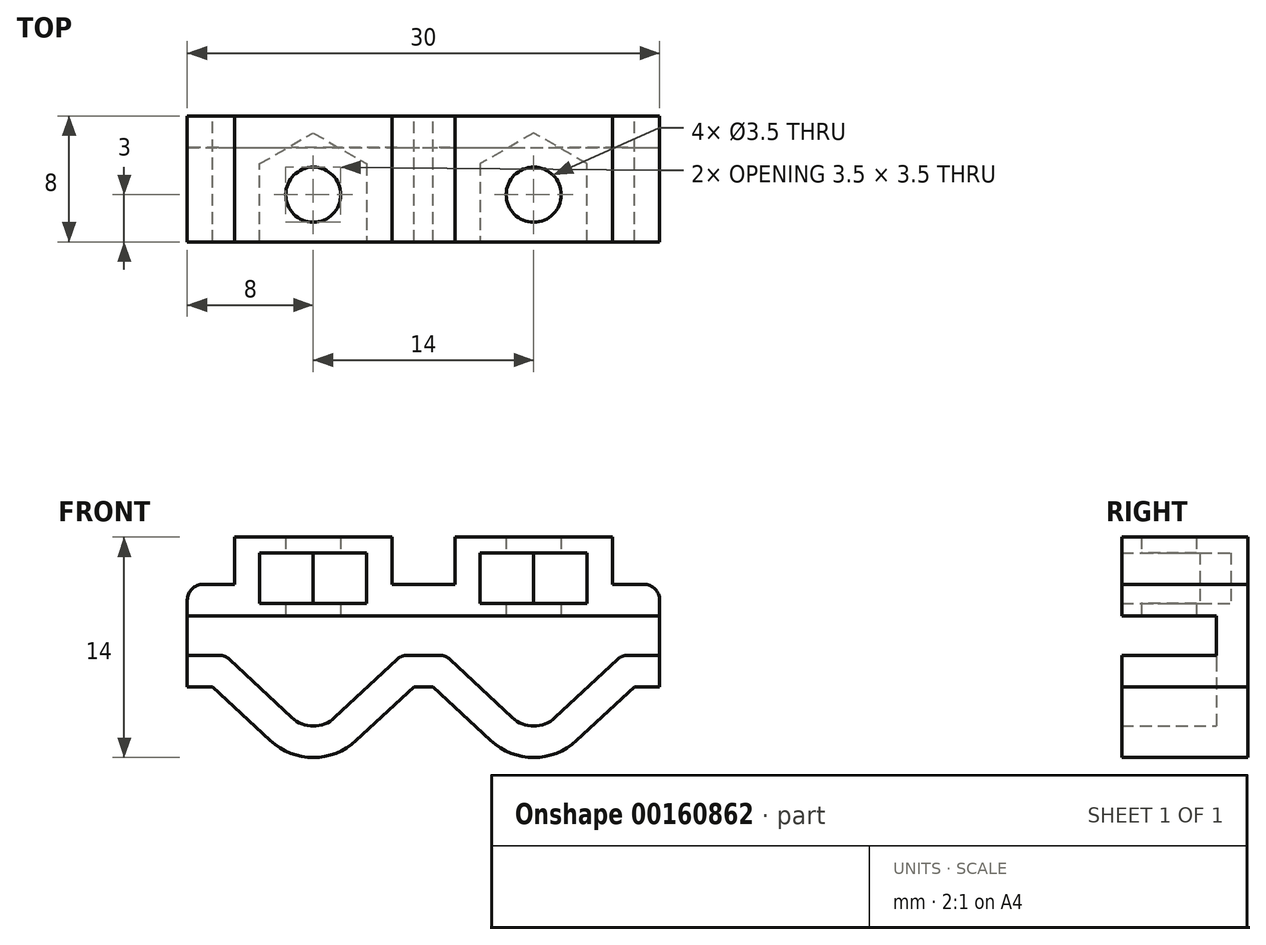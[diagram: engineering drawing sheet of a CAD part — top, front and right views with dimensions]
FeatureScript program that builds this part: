
annotation { "Feature Type Name" : "Feature", "Feature Type Description" : "" }
export const myFeature = defineFeature(function(context is Context, id is Id, definition is map)
    precondition{}
    {
        {
            var Q0;
            Q0=qCreatedBy(makeId("Front.planeOp"),FACE);
            var sketch = newSketch(context, id + "F0", { "sketchPlane" : qUnion([Q0])});
            skLineSegment(sketch, "E0", {"start": v(13, 0) * mm, "end": v(15, 0) * mm});
            skLineSegment(sketch, "E1", {"start": v(15, 0) * mm, "end": v(15, -2) * mm});
            skLineSegment(sketch, "E2", {"start": v(0, 0) * mm, "end": v(1, 0) * mm});
            skArc(sketch, "E3", {"start": v(13, 0) * mm, "mid": v(12.63, -0.07) * mm, "end": v(12.32, -0.27) * mm});
            skArc(sketch, "E4", {"start": v(1.68, -0.27) * mm, "mid": v(1.37, -0.07) * mm, "end": v(1, 0) * mm});
            skLineSegment(sketch, "E5", {"start": v(0, 2.5) * mm, "end": v(1, 2.5) * mm});
            skLineSegment(sketch, "E6", {"start": v(13, 2.5) * mm, "end": v(15, 2.5) * mm});
            skLineSegment(sketch, "E7", {"start": v(1, 2.5) * mm, "end": v(13, 2.5) * mm});
            skLineSegment(sketch, "E8", {"start": v(1.68, -0.27) * mm, "end": v(5.63, -3.96) * mm});
            skLineSegment(sketch, "E9", {"start": v(12.32, -0.27) * mm, "end": v(8.37, -3.96) * mm});
            skArc(sketch, "E10", {"start": v(5.63, -3.96) * mm, "mid": v(7, -4.5) * mm, "end": v(8.37, -3.96) * mm});
            skPoint(sketch, "E11", {"position": v(7, -4.5) * mm});
            skLineSegment(sketch, "E12", {"start": v(15, 2.5) * mm, "end": v(15, 3.5) * mm});
            skLineSegment(sketch, "E13", {"start": v(14, 4.5) * mm, "end": v(12, 4.5) * mm});
            skPoint(sketch, "E14.visualSharp", {"position": v(15, 4.5) * mm});
            skArc(sketch, "E14.filletArc", {"start": v(15, 3.5) * mm, "mid": v(14.7, 4.2) * mm, "end": v(14, 4.5) * mm});
            skLineSegment(sketch, "E15", {"start": v(2, 4.5) * mm, "end": v(2, 7.5) * mm});
            skLineSegment(sketch, "E16", {"start": v(2, 7.5) * mm, "end": v(12, 7.5) * mm});
            skLineSegment(sketch, "E17", {"start": v(12, 7.5) * mm, "end": v(12, 4.5) * mm});
            skPoint(sketch, "E18", {"position": v(7, 7.5) * mm});
            skLineSegment(sketch, "E19.trimOffspring", {"start": v(2, 4.5) * mm, "end": v(0, 4.5) * mm});
            skArc(sketch, "E20.0", {"start": v(4.27, -5.42) * mm, "mid": v(7, -6.5) * mm, "end": v(9.73, -5.42) * mm});
            skLineSegment(sketch, "E21", {"start": v(9.73, -5.42) * mm, "end": v(13.4, -2) * mm});
            skLineSegment(sketch, "E22", {"start": v(4.27, -5.42) * mm, "end": v(0.6, -2) * mm});
            skLineSegment(sketch, "E23", {"start": v(15, -2) * mm, "end": v(13.4, -2) * mm});
            skLineSegment(sketch, "E24", {"start": v(0, -2) * mm, "end": v(0.6, -2) * mm});
            skLineSegment(sketch, "E25", {"start": v(0, 2.5) * mm, "end": v(0, 4.5) * mm});
            skLineSegment(sketch, "E26", {"start": v(0, 0) * mm, "end": v(0, -2) * mm});
            skSolve(sketch);
        }
        {
            var Q0;
            Q0 = qSketchRegion(id + "F0", true);
            extrude(context, id + "F1", {"entities" : qUnion([Q0]), "depth" : 6 * mm});
        }
        {
            var Q0;
            Q0=qCreatedBy(makeId("Front.planeOp"),FACE);
            var sketch = newSketch(context, id + "F2", { "sketchPlane" : qUnion([Q0])});
            skLineSegment(sketch, "E27", {"start": v(15, -2) * mm, "end": v(15, 3.5) * mm});
            skLineSegment(sketch, "E28", {"start": v(14, 4.5) * mm, "end": v(12, 4.5) * mm});
            skLineSegment(sketch, "E29", {"start": v(12, 4.5) * mm, "end": v(12, 7.5) * mm});
            skLineSegment(sketch, "E30", {"start": v(12, 7.5) * mm, "end": v(2, 7.5) * mm});
            skLineSegment(sketch, "E31", {"start": v(2, 7.5) * mm, "end": v(2, 4.5) * mm});
            skLineSegment(sketch, "E32", {"start": v(2, 4.5) * mm, "end": v(0, 4.5) * mm});
            skLineSegment(sketch, "E33", {"start": v(0, 4.5) * mm, "end": v(0, -2) * mm});
            skLineSegment(sketch, "E34", {"start": v(0, -2) * mm, "end": v(0.6, -2) * mm});
            skLineSegment(sketch, "E35", {"start": v(0.6, -2) * mm, "end": v(4.27, -5.42) * mm});
            skLineSegment(sketch, "E36", {"start": v(15, -2) * mm, "end": v(13.4, -2) * mm});
            skLineSegment(sketch, "E37", {"start": v(13.4, -2) * mm, "end": v(9.73, -5.42) * mm});
            skArc(sketch, "E38", {"start": v(15, 3.5) * mm, "mid": v(14.7, 4.2) * mm, "end": v(14, 4.5) * mm});
            skArc(sketch, "E39", {"start": v(4.27, -5.42) * mm, "mid": v(7, -6.5) * mm, "end": v(9.73, -5.42) * mm});
            skSolve(sketch);
        }
        {
            var Q0;
            Q0 = qSketchRegion(id + "F2", true);
            extrude(context, id + "F3", {"entities" : qUnion([Q0]), "operationType" : NewBodyOperationType.ADD, "oppositeDirection" : true, "depth" : 2 * mm});
        }
        {
            var Q0;
            Q0=makeQuery(id+"F1.opExtrude","SWEPT_FACE",FACE,{"disambiguationData":[OSD([sQuery(id+"F0.wireOp",EDGE,"E5"),sQuery(id+"F0.wireOp",EDGE,"E6"),sQuery(id+"F0.wireOp",EDGE,"E7")])]});
            cPlane(context, id + "F4", {"entities" : qUnion([Q0]), "cplaneType" : CPlaneType.OFFSET, "offset" : 0.8 * mm, "oppositeDirection" : true, "width" : 150 * mm, "height" : 150 * mm});
        }
        {
            var Q0;
            Q0=qCreatedBy(id+"F4.planeOp",FACE);
            var sketch = newSketch(context, id + "F5", { "sketchPlane" : qUnion([Q0])});
            skPoint(sketch, "E40", {"position": v(7, 0) * mm});
            skPoint(sketch, "E41", {"position": v(7, 6) * mm});
            skLineSegment(sketch, "E42", {"start": v(7, 0) * mm, "end": v(7, 6) * mm, "construction": true});
            skPoint(sketch, "E43", {"position": v(7, 3) * mm});
            skCircle(sketch, "E44.cCircle", {"center": v(7, 3) * mm, "radius": 3.4 * mm, "construction": true});
            skLineSegment(sketch, "E44.0", {"start": v(10.4, 1.04) * mm, "end": v(7, -0.93) * mm});
            skLineSegment(sketch, "E44.1", {"start": v(7, -0.93) * mm, "end": v(3.6, 1.04) * mm});
            skLineSegment(sketch, "E44.2", {"start": v(3.6, 1.04) * mm, "end": v(3.6, 4.96) * mm});
            skLineSegment(sketch, "E44.3", {"start": v(3.6, 4.96) * mm, "end": v(7, 6.93) * mm, "construction": true});
            skLineSegment(sketch, "E44.4", {"start": v(7, 6.93) * mm, "end": v(10.4, 4.96) * mm, "construction": true});
            skLineSegment(sketch, "E44.5", {"start": v(10.4, 4.96) * mm, "end": v(10.4, 1.04) * mm});
            skPoint(sketch, "E44.0.midPoint", {"position": v(8.7, 0.06) * mm});
            skLineSegment(sketch, "E45", {"start": v(3.6, 4.96) * mm, "end": v(3.6, 11.37) * mm});
            skLineSegment(sketch, "E46", {"start": v(3.6, 11.37) * mm, "end": v(10.4, 11.37) * mm});
            skLineSegment(sketch, "E47", {"start": v(10.4, 11.37) * mm, "end": v(10.4, 4.96) * mm});
            skSolve(sketch);
        }
        {
            var Q0;
            Q0 = qSketchRegion(id + "F5", true);
            extrude(context, id + "F6", {"entities" : qUnion([Q0]), "operationType" : NewBodyOperationType.REMOVE, "oppositeDirection" : true, "depth" : 3.2 * mm});
        }
        {
            var Q0;
            Q0=makeQuery(id+"F6.boolean.opBoolean","COPY",FACE,{"derivedFrom":makeQuery(id+"F6.opExtrude","CAP_FACE",FACE,{"disambiguationData":[OSD([sQuery(id+"F5.wireOp",EDGE,"E44.0"),sQuery(id+"F5.wireOp",EDGE,"E44.1"),sQuery(id+"F5.wireOp",EDGE,"E44.2"),sQuery(id+"F5.wireOp",EDGE,"E44.5"),sQuery(id+"F5.wireOp",EDGE,"E45"),sQuery(id+"F5.wireOp",EDGE,"E46"),sQuery(id+"F5.wireOp",EDGE,"E47")])],"isStart":true})});
            var sketch = newSketch(context, id + "F7", { "sketchPlane" : qUnion([Q0])});
            skCircle(sketch, "E48", {"center": v(7, -3) * mm, "radius": 1.75 * mm});
            skSolve(sketch);
        }
        {
            var Q0;
            Q0 = qSketchRegion(id + "F7", true);
            var Q1;
            Q1=makeQuery(id+"F3.boolean.opBoolean","MERGE",FACE,{"derivedFrom":[makeQuery(id+"F1.opExtrude","SWEPT_FACE",FACE,{"disambiguationData":[OSD([sQuery(id+"F0.wireOp",EDGE,"E16")])]}),makeQuery(id+"F3.opExtrude","SWEPT_FACE",FACE,{"disambiguationData":[OSD([sQuery(id+"F2.wireOp",EDGE,"E30")])]})]});
            var Q2;
            Q2=makeQuery(id+"F1.opExtrude","SWEPT_FACE",FACE,{"disambiguationData":[OSD([sQuery(id+"F0.wireOp",EDGE,"E5"),sQuery(id+"F0.wireOp",EDGE,"E6"),sQuery(id+"F0.wireOp",EDGE,"E7")])]});
            extrude(context, id + "F8", {"entities" : qUnion([Q0]), "operationType" : NewBodyOperationType.REMOVE, "endBound" : BoundingType.UP_TO_SURFACE, "endBoundEntityFace" : qUnion([Q1]), "depth" : 25 * mm, "hasSecondDirection" : true, "secondDirectionBound" : BoundingType.UP_TO_SURFACE, "secondDirectionOppositeDirection" : true, "secondDirectionBoundEntityFace" : qUnion([Q2]), "secondDirectionDepth" : 25 * mm});
        }
        {
            var Q0;
            Q0=makeQuery(id+"F1.opExtrude","SWEPT_BODY",BODY,{"disambiguationData":[OSD([sQuery(id+"F0.wireOp",EDGE,"E0"),sQuery(id+"F0.wireOp",EDGE,"E1"),sQuery(id+"F0.wireOp",EDGE,"E2"),sQuery(id+"F0.wireOp",EDGE,"E3"),sQuery(id+"F0.wireOp",EDGE,"E4"),sQuery(id+"F0.wireOp",EDGE,"E8"),sQuery(id+"F0.wireOp",EDGE,"E9"),sQuery(id+"F0.wireOp",EDGE,"E10"),sQuery(id+"F0.wireOp",EDGE,"E20.0"),sQuery(id+"F0.wireOp",EDGE,"E21"),sQuery(id+"F0.wireOp",EDGE,"E22"),sQuery(id+"F0.wireOp",EDGE,"E23"),sQuery(id+"F0.wireOp",EDGE,"E24"),sQuery(id+"F0.wireOp",EDGE,"E26")])]});
            var Q1;
            Q1=qCreatedBy(makeId("Right.planeOp"),FACE);
            mirror(context, id + "F9", {"operationType" : NewBodyOperationType.ADD, "entities" : qUnion([Q0]), "mirrorPlane" : qUnion([Q1])});
        }
    });
